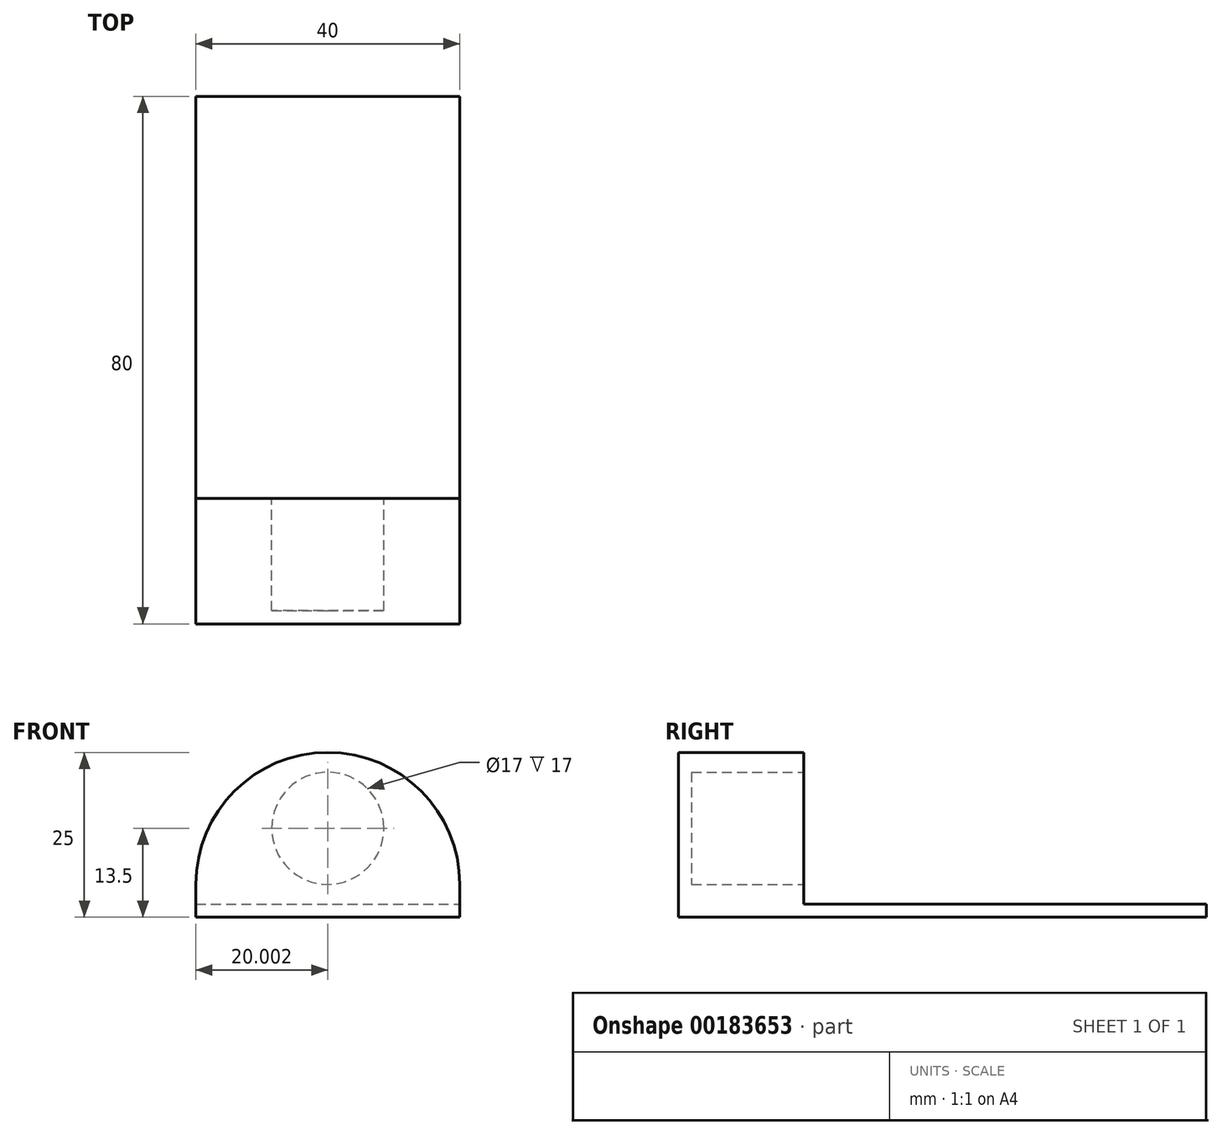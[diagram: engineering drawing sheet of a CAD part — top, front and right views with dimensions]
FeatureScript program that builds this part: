
annotation { "Feature Type Name" : "Feature", "Feature Type Description" : "" }
export const myFeature = defineFeature(function(context is Context, id is Id, definition is map)
    precondition{}
    {
        {
            var Q0;
            Q0=qCreatedBy(makeId("Top.planeOp"),FACE);
            var sketch = newSketch(context, id + "F0", { "sketchPlane" : qUnion([Q0])});
            skLineSegment(sketch, "E0.bottom", {"start": v(-22.85, 59.12) * mm, "end": v(17.15, 59.12) * mm});
            skLineSegment(sketch, "E0.top", {"start": v(-22.85, -20.88) * mm, "end": v(17.15, -20.88) * mm});
            skLineSegment(sketch, "E0.left", {"start": v(-22.85, 59.12) * mm, "end": v(-22.85, -20.88) * mm});
            skLineSegment(sketch, "E0.right", {"start": v(17.15, 59.12) * mm, "end": v(17.15, -20.88) * mm});
            skLineSegment(sketch, "E1", {"start": v(-22.85, -1.88) * mm, "end": v(17.15, -1.88) * mm});
            skSolve(sketch);
        }
        {
            var Q0;
            {var subQ0=sQuery(id+"F0.wireOp",EDGE,"E0.bottom");Q0=makeQuery(id+"F0.imprint","IMPRINT",FACE,{"disambiguationData":[TD([[makeQuery(id+"F0.imprint","IMPRINT",EDGE,{"derivedFrom":subQ0}),-1.0]])]});}
            extrude(context, id + "F1", {"entities" : qUnion([Q0]), "depth" : 2 * mm});
        }
        {
            var Q0;
            {var subQ0=sQuery(id+"F0.wireOp",EDGE,"E0.top");Q0=makeQuery(id+"F0.imprint","IMPRINT",FACE,{"disambiguationData":[TD([[makeQuery(id+"F0.imprint","IMPRINT",EDGE,{"derivedFrom":subQ0}),1.0]])]});}
            extrude(context, id + "F2", {"entities" : qUnion([Q0]), "operationType" : NewBodyOperationType.ADD, "depth" : 25 * mm});
        }
        {
            var Q0;
            Q0=makeQuery(id+"F2.opExtrude","SWEPT_FACE",FACE,{"disambiguationData":[OSD([sQuery(id+"F0.wireOp",EDGE,"E1")])]});
            var sketch = newSketch(context, id + "F3", { "sketchPlane" : qUnion([Q0])});
            skCircle(sketch, "E2", {"center": v(2.85, 13.5) * mm, "radius": 8.5 * mm});
            skPoint(sketch, "E2.centerSnap0", {"position": v(2.85, 25) * mm});
            skPoint(sketch, "E2.centerSnap1", {"position": v(22.85, 13.5) * mm});
            skSolve(sketch);
        }
        {
            var Q0;
            Q0 = qSketchRegion(id + "F3", true);
            extrude(context, id + "F4", {"entities" : qUnion([Q0]), "operationType" : NewBodyOperationType.REMOVE, "oppositeDirection" : true, "depth" : 17 * mm});
        }
        {
            var Q0;
            Q0=makeQuery(id+"F2.opExtrude","CAP_EDGE",EDGE,{"disambiguationData":[OSD([sQuery(id+"F0.wireOp",EDGE,"E0.right")])],"isStart":false});
            var Q1;
            Q1=makeQuery(id+"F2.opExtrude","CAP_EDGE",EDGE,{"disambiguationData":[OSD([sQuery(id+"F0.wireOp",EDGE,"E0.left")])],"isStart":false});
            fillet(context, id + "F5", {"entities" : qUnion([Q0, Q1]), "radius" : 20 * mm, "tangentPropagation" : true, "allowEdgeOverflow" : false});
        }
    });
